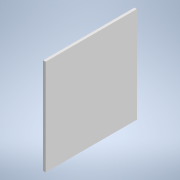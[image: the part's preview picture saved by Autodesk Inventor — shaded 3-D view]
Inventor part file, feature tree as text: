
AUTODESK INVENTOR PART (.ipt)
format: ipt  version: 2020 (Build 240168000, 168)  size: 89,600 bytes
history: native  units: mm
features: extrude x1, sketch x1
ambient origin geometry x8: Origin, YZ Plane, XZ Plane, XY Plane, X Axis, Y Axis, Z Axis, Center Point
bodies: Solid1 (feature_tree)
feature tree (2):
  extrude  "Extrusion1"  Depth=581.0mm
  sketch  "Sketch1"  dims[d0=610.0mm d1=581.0mm d2=16.0mm d3=0.0mm]
